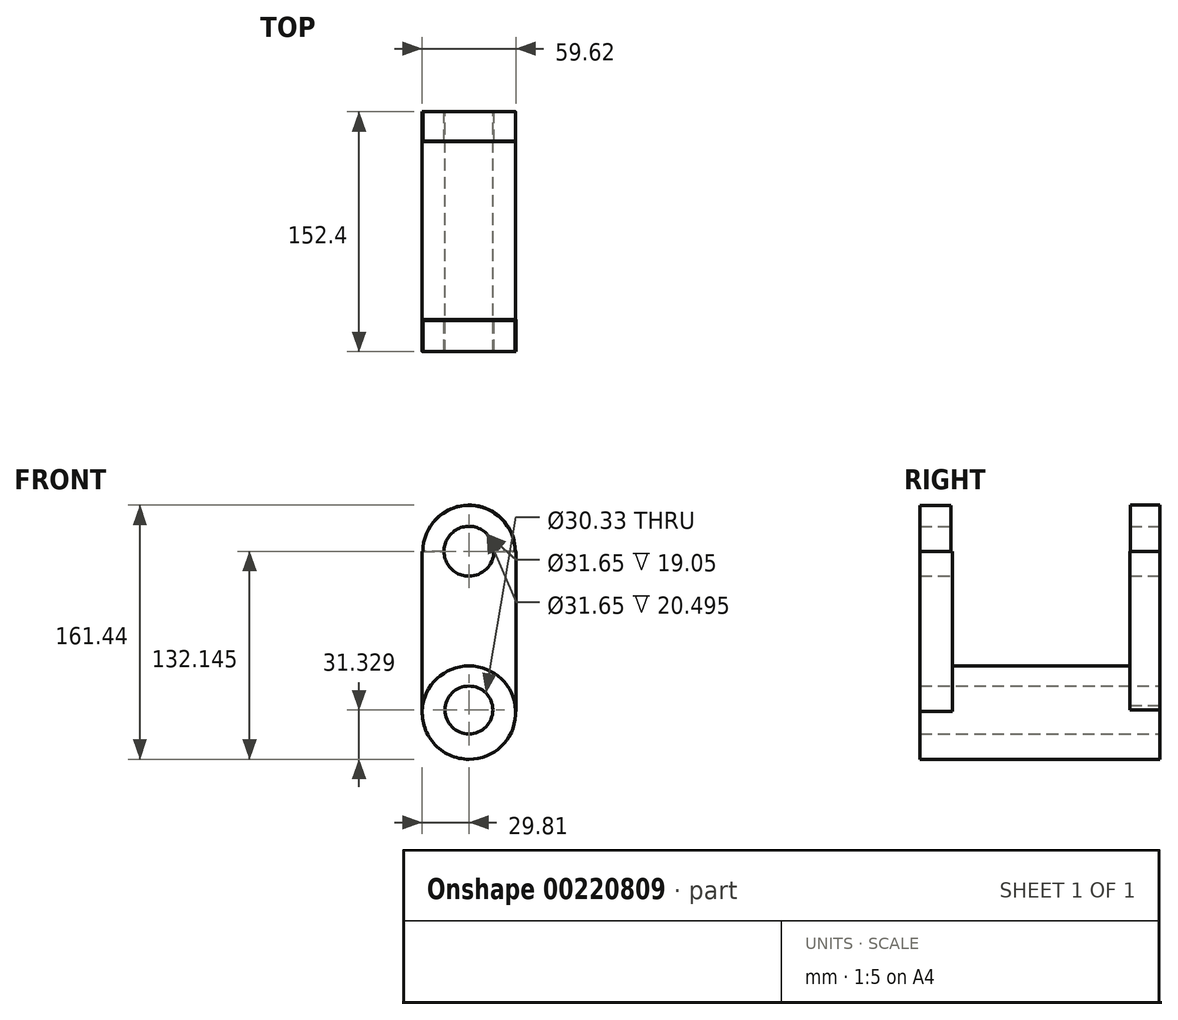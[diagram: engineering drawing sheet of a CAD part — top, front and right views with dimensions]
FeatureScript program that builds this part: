
annotation { "Feature Type Name" : "Feature", "Feature Type Description" : "" }
export const myFeature = defineFeature(function(context is Context, id is Id, definition is map)
    precondition{}
    {
        {
            var Q0;
            Q0=qCreatedBy(makeId("Front.planeOp"),FACE);
            var sketch = newSketch(context, id + "F0", { "sketchPlane" : qUnion([Q0])});
            skCircle(sketch, "E0", {"center": v(0, -51.47) * mm, "radius": 29.67 * mm});
            skSolve(sketch);
        }
        {
            var Q0;
            Q0=makeQuery(id+"F0.imprint","IMPRINT",FACE,{"disambiguationData":[TD([[makeQuery(id+"F0.imprint","IMPRINT",EDGE,{"derivedFrom":sQuery(id+"F0.wireOp",EDGE,"E0")}),1.0]])]});
            extrude(context, id + "F1", {"entities" : qUnion([Q0]), "depth" : 38.1 * mm});
        }
        {
            var Q0;
            Q0=makeQuery(id+"F1.opExtrude","CAP_FACE",FACE,{"disambiguationData":[OSD([sQuery(id+"F0.wireOp",EDGE,"E0")])],"isStart":false});
            extrude(context, id + "F2", {"entities" : qUnion([Q0]), "operationType" : NewBodyOperationType.ADD, "depth" : 38.1 * mm});
        }
        {
            var Q0;
            Q0=makeQuery(id+"F1.opExtrude","CAP_FACE",FACE,{"disambiguationData":[OSD([sQuery(id+"F0.wireOp",EDGE,"E0")])],"isStart":true});
            extrude(context, id + "F3", {"entities" : qUnion([Q0]), "operationType" : NewBodyOperationType.ADD, "depth" : 76.2 * mm});
        }
        {
            var Q0;
            Q0=qCreatedBy(makeId("Top.planeOp"),FACE);
            var sketch = newSketch(context, id + "F4", { "sketchPlane" : qUnion([Q0])});
            skLineSegment(sketch, "E1.bottom", {"start": v(-29.81, -76.16) * mm, "end": v(29.81, -76.16) * mm});
            skLineSegment(sketch, "E1.top", {"start": v(-29.81, -55.66) * mm, "end": v(29.81, -55.66) * mm});
            skLineSegment(sketch, "E1.left", {"start": v(-29.81, -76.16) * mm, "end": v(-29.81, -55.66) * mm});
            skLineSegment(sketch, "E1.right", {"start": v(29.81, -76.16) * mm, "end": v(29.81, -55.66) * mm});
            skSolve(sketch);
        }
        {
            var Q0;
            Q0=makeQuery(id+"F4.imprint","IMPRINT",FACE,{"disambiguationData":[TD([[makeQuery(id+"F4.imprint","IMPRINT",EDGE,{"derivedFrom":sQuery(id+"F4.wireOp",EDGE,"E1.bottom")}),1.0]])]});
            extrude(context, id + "F5", {"entities" : qUnion([Q0]), "operationType" : NewBodyOperationType.ADD, "oppositeDirection" : true, "depth" : 50.8 * mm});
        }
        {
            var Q0;
            Q0=makeQuery(id+"F5.opExtrude","CAP_FACE",FACE,{"disambiguationData":[OSD([sQuery(id+"F4.wireOp",EDGE,"E1.bottom"),sQuery(id+"F4.wireOp",EDGE,"E1.top"),sQuery(id+"F4.wireOp",EDGE,"E1.left"),sQuery(id+"F4.wireOp",EDGE,"E1.right")])],"isStart":true});
            extrude(context, id + "F6", {"entities" : qUnion([Q0]), "operationType" : NewBodyOperationType.ADD, "depth" : 50.8 * mm});
        }
        {
            var Q0;
            {var subQ0=sQuery(id+"F4.wireOp",EDGE,"E1.bottom");Q0=makeQuery(id+"F6.boolean.opBoolean","MERGE",FACE,{"derivedFrom":[makeQuery(id+"F5.opExtrude","SWEPT_FACE",FACE,{"disambiguationData":[OSD([subQ0])]}),makeQuery(id+"F6.opExtrude","SWEPT_FACE",FACE,{"disambiguationData":[OSD([subQ0])]})]});}
            var sketch = newSketch(context, id + "F7", { "sketchPlane" : qUnion([Q0])});
            skCircle(sketch, "E2", {"center": v(0, 50.8) * mm, "radius": 29.3 * mm});
            skSolve(sketch);
        }
        {
            var Q0;
            {var subQ0=sQuery(id+"F7.wireOp",EDGE,"E2");var subQ1=makeQuery(id+"F6.opExtrude","CAP_EDGE",EDGE,{"disambiguationData":[OSD([sQuery(id+"F4.wireOp",EDGE,"E1.bottom")])],"isStart":false});var subQ2=makeQuery(id+"F7.imprint","INTERSECT",VERTEX,{"disambiguationData":[OD(0.0)],"derivedFrom":[subQ1,subQ0]});Q0=makeQuery(id+"F7.imprint","IMPRINT",FACE,{"disambiguationData":[TD([[makeQuery(id+"F7.imprint","IMPRINT",EDGE,{"disambiguationData":[TD([[subQ2,1.0]])],"derivedFrom":subQ0}),1.0]])]});}
            extrude(context, id + "F8", {"entities" : qUnion([Q0]), "operationType" : NewBodyOperationType.ADD, "oppositeDirection" : true, "depth" : 19.56 * mm});
        }
        {
            var Q0;
            Q0=makeQuery(id+"F3.opExtrude","CAP_FACE",FACE,{"disambiguationData":[OSD([sQuery(id+"F0.wireOp",EDGE,"E0")])],"isStart":false});
            var sketch = newSketch(context, id + "F9", { "sketchPlane" : qUnion([Q0])});
            skLineSegment(sketch, "E3.bottom", {"start": v(-29.63, -49.81) * mm, "end": v(29.35, -49.81) * mm});
            skLineSegment(sketch, "E3.top", {"start": v(-29.63, 51) * mm, "end": v(29.35, 51) * mm});
            skLineSegment(sketch, "E3.left", {"start": v(-29.63, -49.81) * mm, "end": v(-29.63, 51) * mm});
            skLineSegment(sketch, "E3.right", {"start": v(29.35, -49.81) * mm, "end": v(29.35, 51) * mm});
            skSolve(sketch);
        }
        {
            var Q0;
            {var subQ0=sQuery(id+"F9.wireOp",EDGE,"E3.top");Q0=makeQuery(id+"F9.imprint","IMPRINT",FACE,{"disambiguationData":[TD([[makeQuery(id+"F9.imprint","IMPRINT",EDGE,{"derivedFrom":subQ0}),-1.0]])]});}
            extrude(context, id + "F10", {"entities" : qUnion([Q0]), "operationType" : NewBodyOperationType.ADD, "oppositeDirection" : true, "depth" : 19.05 * mm});
        }
        {
            var Q0;
            {var subQ0=sQuery(id+"F0.wireOp",EDGE,"E0");Q0=makeQuery(id+"F10.boolean.opBoolean","MERGE",FACE,{"derivedFrom":[makeQuery(id+"F3.opExtrude","CAP_FACE",FACE,{"disambiguationData":[OSD([subQ0])],"isStart":false}),makeQuery(id+"F10.opExtrude","CAP_FACE",FACE,{"disambiguationData":[OSD([subQ0,sQuery(id+"F9.wireOp",EDGE,"E3.top"),sQuery(id+"F9.wireOp",EDGE,"E3.left"),sQuery(id+"F9.wireOp",EDGE,"E3.right")])],"isStart":true})]});}
            var sketch = newSketch(context, id + "F11", { "sketchPlane" : qUnion([Q0])});
            skCircle(sketch, "E4", {"center": v(-0.14, 51) * mm, "radius": 29.3 * mm});
            skSolve(sketch);
        }
        {
            var Q0;
            {var subQ0=sQuery(id+"F11.wireOp",EDGE,"E4");var subQ1=makeQuery(id+"F10.opExtrude","CAP_EDGE",EDGE,{"disambiguationData":[OSD([sQuery(id+"F9.wireOp",EDGE,"E3.top")])],"isStart":true});var subQ2=makeQuery(id+"F11.imprint","INTERSECT",VERTEX,{"disambiguationData":[OD(0.0)],"derivedFrom":[subQ1,subQ0]});Q0=makeQuery(id+"F11.imprint","IMPRINT",FACE,{"disambiguationData":[TD([[makeQuery(id+"F11.imprint","IMPRINT",EDGE,{"disambiguationData":[TD([[subQ2,1.0]])],"derivedFrom":subQ0}),1.0]])]});}
            extrude(context, id + "F12", {"entities" : qUnion([Q0]), "operationType" : NewBodyOperationType.ADD, "oppositeDirection" : true, "depth" : 18.8 * mm});
        }
        {
            var Q0;
            {var subQ0=sQuery(id+"F9.wireOp",EDGE,"E3.top");var subQ1=sQuery(id+"F0.wireOp",EDGE,"E0");Q0=makeQuery(id+"F12.boolean.opBoolean","MERGE",FACE,{"derivedFrom":[makeQuery(id+"F10.boolean.opBoolean","MERGE",FACE,{"derivedFrom":[makeQuery(id+"F3.opExtrude","CAP_FACE",FACE,{"disambiguationData":[OSD([subQ1])],"isStart":false}),makeQuery(id+"F10.opExtrude","CAP_FACE",FACE,{"disambiguationData":[OSD([subQ1,subQ0,sQuery(id+"F9.wireOp",EDGE,"E3.left"),sQuery(id+"F9.wireOp",EDGE,"E3.right")])],"isStart":true})]}),makeQuery(id+"F12.opExtrude","CAP_FACE",FACE,{"disambiguationData":[OSD([subQ0,sQuery(id+"F11.wireOp",EDGE,"E4")])],"isStart":true})]});}
            var sketch = newSketch(context, id + "F13", { "sketchPlane" : qUnion([Q0])});
            skCircle(sketch, "E5", {"center": v(0, -49.81) * mm, "radius": 15.17 * mm});
            skSolve(sketch);
        }
        {
            var Q0;
            Q0=makeQuery(id+"F13.imprint","IMPRINT",FACE,{"disambiguationData":[TD([[makeQuery(id+"F13.imprint","IMPRINT",EDGE,{"derivedFrom":sQuery(id+"F13.wireOp",EDGE,"E5")}),1.0]])]});
            extrude(context, id + "F14", {"entities" : qUnion([Q0]), "operationType" : NewBodyOperationType.REMOVE, "oppositeDirection" : true, "depth" : 203.2 * mm});
        }
        {
            var Q0;
            {var subQ0=sQuery(id+"F9.wireOp",EDGE,"E3.top");var subQ1=sQuery(id+"F0.wireOp",EDGE,"E0");Q0=makeQuery(id+"F12.boolean.opBoolean","MERGE",FACE,{"derivedFrom":[makeQuery(id+"F10.boolean.opBoolean","MERGE",FACE,{"derivedFrom":[makeQuery(id+"F3.opExtrude","CAP_FACE",FACE,{"disambiguationData":[OSD([subQ1])],"isStart":false}),makeQuery(id+"F10.opExtrude","CAP_FACE",FACE,{"disambiguationData":[OSD([subQ1,subQ0,sQuery(id+"F9.wireOp",EDGE,"E3.left"),sQuery(id+"F9.wireOp",EDGE,"E3.right")])],"isStart":true})]}),makeQuery(id+"F12.opExtrude","CAP_FACE",FACE,{"disambiguationData":[OSD([subQ0,sQuery(id+"F11.wireOp",EDGE,"E4")])],"isStart":true})]});}
            var sketch = newSketch(context, id + "F15", { "sketchPlane" : qUnion([Q0])});
            skCircle(sketch, "E6", {"center": v(0, 51) * mm, "radius": 15.82 * mm});
            skSolve(sketch);
        }
        {
            var Q0;
            Q0=makeQuery(id+"F15.imprint","IMPRINT",FACE,{"disambiguationData":[TD([[makeQuery(id+"F15.imprint","IMPRINT",EDGE,{"derivedFrom":sQuery(id+"F15.wireOp",EDGE,"E6")}),1.0]])]});
            extrude(context, id + "F16", {"entities" : qUnion([Q0]), "operationType" : NewBodyOperationType.REMOVE, "oppositeDirection" : true, "depth" : 177.8 * mm});
        }
    });
